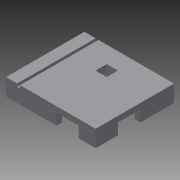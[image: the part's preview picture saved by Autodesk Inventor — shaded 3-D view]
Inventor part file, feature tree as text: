
AUTODESK INVENTOR PART (.ipt)
format: ipt  version: 2014 SP1 (Build 180222100, 222)  size: 135,168 bytes
history: native  units: in
note: dims shown in document units (in); Inventor stores cm internally (conversion verified against a paired STEP export)
features: extrude x6, sketch x6
ambient origin geometry x8: Origin, YZ Plane, XZ Plane, XY Plane, X Axis, Y Axis, Z Axis, Center Point
bodies: Solid1 (feature_tree)
feature tree (12):
  extrude  "Extrusion1"  Depth=1.75in
  extrude  "Extrusion4"  Depth=0.125in TaperAngle=0.0deg
  extrude  "Extrusion5"  Depth=1.125in
  extrude  "Extrusion6"  Depth=0.25in
  sketch  "Sketch1"  dims[d0=2.0in d1=1.75in]
  sketch  "Sketch4"  dims[d18=0.0in d20=1.125in]
  sketch  "Sketch5"  dims[d21=1.625in d22=0.25in]
  sketch  "Sketch6"  dims[d23=0.5in d24=1.0in d25=0.125in d26=0.0in d27=0.25in d28=0.875in d29=1.125in d30=0.375in d31=0.625in d32=0.125in d33=0.0in d34=0.0625in d35=0.25in d36=0.0625in d37=0.0in]
  sketch  "Sketch2"  dims[d2=0.125in d3=0.0in]
  sketch  "Sketch3"  dims[d4=0.125in d5=0.125in d6=0.125in d7=0.125in d9=0.0in d10=0.25in d15=0.0in d16=0.125in]
  extrude  "Extrusion2"  Depth=1.0in
  extrude  "Extrusion3"  Depth=0.125in TaperAngle=0.0deg
